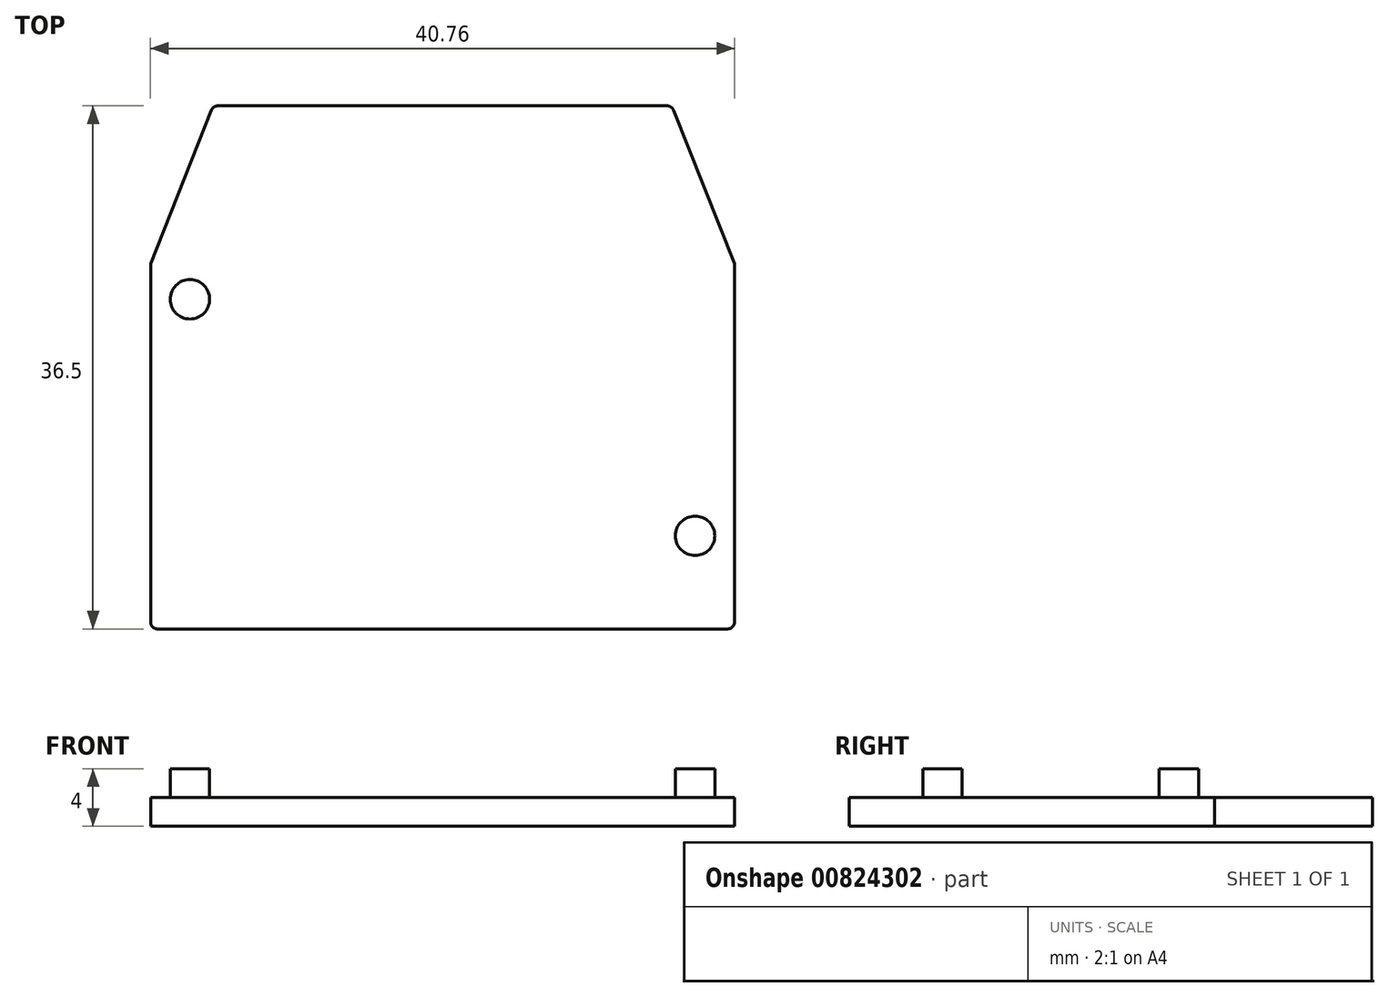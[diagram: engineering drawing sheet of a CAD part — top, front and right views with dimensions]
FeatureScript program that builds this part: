
annotation { "Feature Type Name" : "Feature", "Feature Type Description" : "" }
export const myFeature = defineFeature(function(context is Context, id is Id, definition is map)
    precondition{}
    {
        {
            var Q0;
            Q0=qCreatedBy(makeId("Top.planeOp"),FACE);
            var sketch = newSketch(context, id + "F0", { "sketchPlane" : qUnion([Q0])});
            skLineSegment(sketch, "E0", {"start": v(-20.37, 0) * mm, "end": v(20.38, 0) * mm});
            skLineSegment(sketch, "E1", {"start": v(20.37, 0) * mm, "end": v(20.37, 25.5) * mm});
            skLineSegment(sketch, "E2", {"start": v(20.38, 25.5) * mm, "end": v(16, 36.5) * mm});
            skLineSegment(sketch, "E3", {"start": v(16, 36.5) * mm, "end": v(-16, 36.5) * mm});
            skLineSegment(sketch, "E4", {"start": v(-16, 36.5) * mm, "end": v(-20.38, 25.5) * mm});
            skLineSegment(sketch, "E5", {"start": v(-20.37, 25.5) * mm, "end": v(-20.37, 0) * mm});
            skLineSegment(sketch, "E6", {"start": v(0, 39.94) * mm, "end": v(0, -2.92) * mm, "construction": true});
            skSolve(sketch);
        }
        {
            var Q0;
            Q0=qSketchRegion(id+"F0",true);
            extrude(context, id + "F1", {"entities" : qUnion([Q0]), "depth" : 2 * mm, "offsetDistance" : 25 * mm, "symmetric" : true});
        }
        {
            var Q0;
            Q0=makeQuery(id+"F1.opExtrude","CAP_FACE",FACE,{"disambiguationData":[OSD([sQuery(id+"F0.wireOp",EDGE,"E0"),sQuery(id+"F0.wireOp",EDGE,"E1"),sQuery(id+"F0.wireOp",EDGE,"E2"),sQuery(id+"F0.wireOp",EDGE,"E3"),sQuery(id+"F0.wireOp",EDGE,"E4"),sQuery(id+"F0.wireOp",EDGE,"E5")])],"isStart":false});
            var sketch = newSketch(context, id + "F2", { "sketchPlane" : qUnion([Q0])});
            skCircle(sketch, "E7", {"center": v(17.62, 6.5) * mm, "radius": 1.38 * mm});
            skCircle(sketch, "E8", {"center": v(-17.62, 23) * mm, "radius": 1.38 * mm});
            skSolve(sketch);
        }
        {
            var Q0;
            Q0 = qSketchRegion(id + "F2", true);
            extrude(context, id + "F3", {"entities" : qUnion([Q0]), "operationType" : NewBodyOperationType.ADD, "depth" : 2 * mm, "offsetDistance" : 25 * mm});
        }
        {
            var Q0;
            Q0=makeQuery(id+"F1.opExtrude","SWEPT_EDGE",EDGE,{"disambiguationData":[OSD([sQuery(id+"F0.wireOp",EDGE,"E0"),sQuery(id+"F0.wireOp",EDGE,"E1")])]});
            var Q1;
            Q1=makeQuery(id+"F1.opExtrude","SWEPT_EDGE",EDGE,{"disambiguationData":[OSD([sQuery(id+"F0.wireOp",EDGE,"E0"),sQuery(id+"F0.wireOp",EDGE,"E5")])]});
            var Q2;
            Q2=makeQuery(id+"F1.opExtrude","SWEPT_EDGE",EDGE,{"disambiguationData":[OSD([sQuery(id+"F0.wireOp",EDGE,"E3"),sQuery(id+"F0.wireOp",EDGE,"E4")])]});
            var Q3;
            Q3=makeQuery(id+"F1.opExtrude","SWEPT_EDGE",EDGE,{"disambiguationData":[OSD([sQuery(id+"F0.wireOp",EDGE,"E2"),sQuery(id+"F0.wireOp",EDGE,"E3")])]});
            fillet(context, id + "F4", {"entities" : qUnion([Q0, Q1, Q2, Q3]), "radius" : 0.5 * mm, "tangentPropagation" : true, "allowEdgeOverflow" : false});
        }
    });
